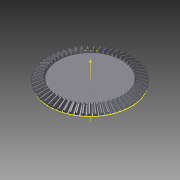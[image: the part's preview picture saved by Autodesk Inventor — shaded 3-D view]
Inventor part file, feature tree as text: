
AUTODESK INVENTOR PART (.ipt)
format: ipt  version: 2014 (Build 180170000, 170)  size: 986,624 bytes
history: native  units: mm
features: other x24, sketch x3, loft x2, pattern_circular x2, extrude x2
ambient origin geometry x6: Origin, XZ Plane, X Axis, Y Axis, Z Axis, Center Point
bodies: Solid1 (feature_tree)
feature tree (33):
  other  "Top Point"
  other  "Mesh Plane2"
  other  "Teeth Body"
  other  "Start Point"
  other  "Tooth Plane"
  other  "Start Sketch"
  other  "End Point"
  other  "3D Sketch Right"
  other  "End Plane Right"
  loft  "Loft Right"
  pattern_circular  "Circular Pattern Right"  Count=2  [1 undecoded]
  other  "3D Sketch Left"
  other  "End Plane Left"
  loft  "Loft Left"
  pattern_circular  "Circular Pattern Left"  [2 undecoded]
  other  "Fix Body"
  extrude  "Extrusion1"  Depth=10.0mm
  extrude  "Extrusion2"  Depth=10.0mm
  other  "Mesh Plane"
  other  "Top Plane"
  other  "Teeth Body Sketch"
  other  "End Plane"
  other  "End Sketch"
  other  "Helical Curve Left"
  other  "End Sketch Left"
  other  "Body Sketch"
  sketch  "Sketch6"  dims[d0=171.0mm d1=168.305803mm]
  other  "Srf1"
  other  "Helical Curve Right"
  other  "End Sketch Right"
  sketch  "Sketch8"  dims[d2=173.245164mm d3=20.0mm]
  sketch  "Sketch9"  dims[d4=31.717949mm d5=90.0deg d7=79.194946mm d8=76.874908mm d9=201.595668mm d11=20.33mm d12=61.811392mm d15=60.00061mm d16=157.344748mm d17=0.0mm d18=90.0deg d19=0.0mm d20=90.0deg d21=570.0mm d22=360.0deg d26=676.499423mm d27=7.607365mm d28=171.0mm d29=-11.872688mm d30=61.811392mm d31=60.00061mm d32=157.344748mm d35=0.0mm d37=0.0mm d39=0.0mm d40=90.0deg d41=570.0mm d42=360.0deg d46=90.0deg d47=90.0deg d48=0.0mm d49=0.0mm d50=90.0deg d51=0.551157mm d52=0.0mm d53=0.0mm d54=0.0mm d56=25.395667mm d57=233.471083mm d58=224.099083mm d59=182.223404mm d60=174.908589mm d61=182.223404mm d62=174.908589mm d65=676.499423mm d66=31.5mm d67=171.0mm d68=-11.872688mm d69=7.607365mm d70=60.00061mm d71=157.344748mm d72=61.811392mm d73=174.908589mm d74=182.223404mm d75=0.0mm d77=0.0mm d79=0.0mm d80=90.0deg d81=570.0mm d82=360.0deg d84=10.0mm d85=20.0mm d86=20.0mm d87=10.0mm d88=0.0mm d89=0.0mm d90=90.0deg d91=90.0deg d92=90.0deg d93=90.0deg d94=95.5mm d95=9.0mm d96=10.0mm d97=0.0mm d98=60.0mm d99=10.0mm d100=0.0mm]
  other  "Pitch Diameter"
note: 3 required parameter values undecoded (feature->parameter linkage not recoverable at this tier; creation-order binding heuristic only, values carry confidence <= 0.55)
